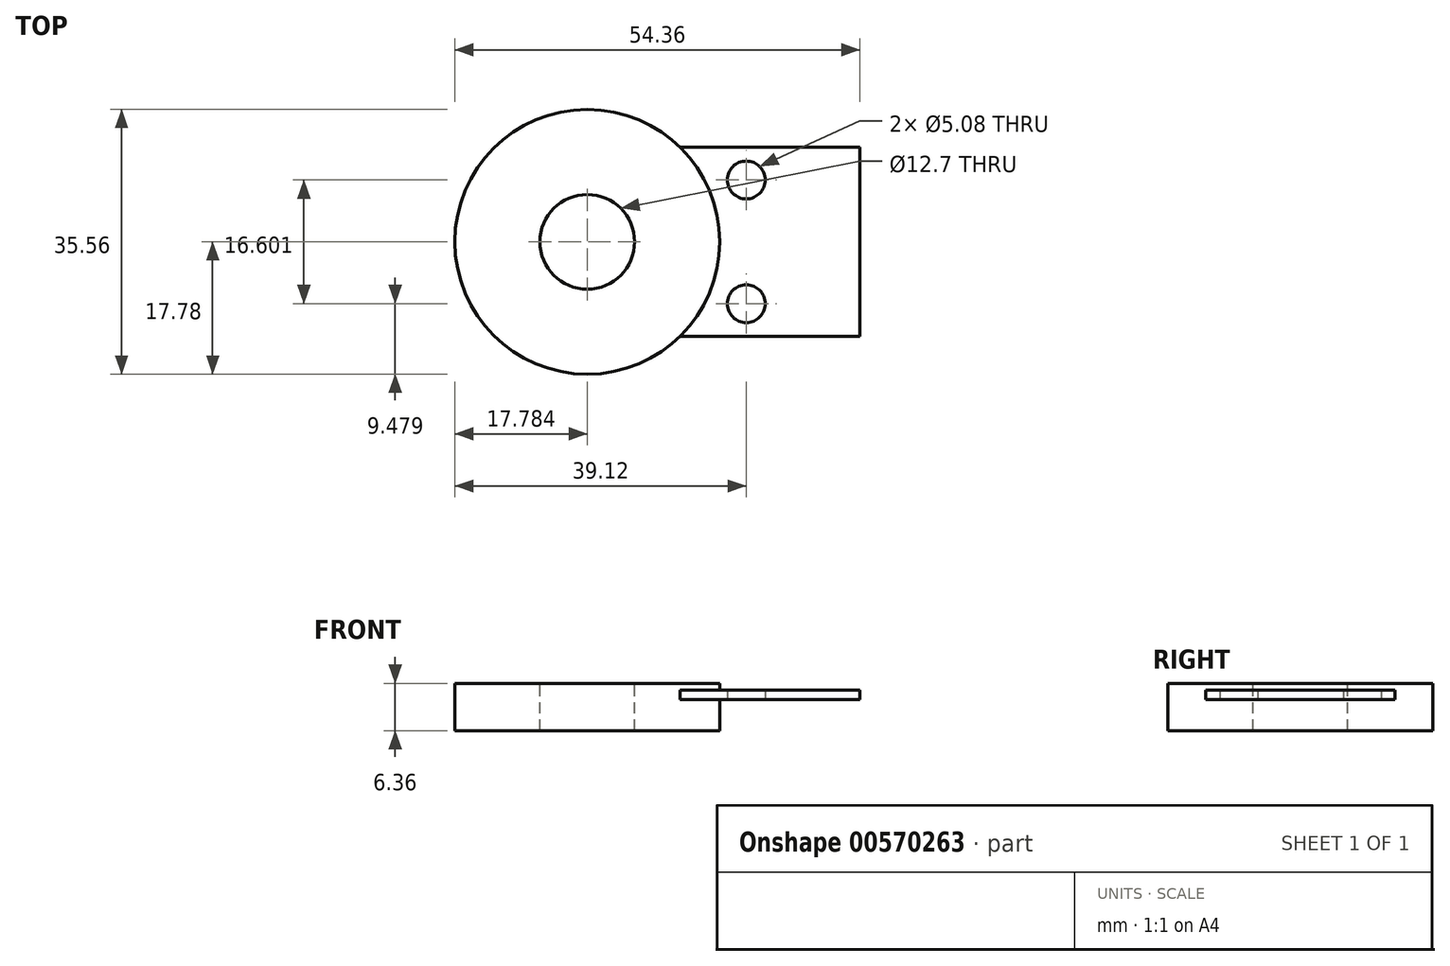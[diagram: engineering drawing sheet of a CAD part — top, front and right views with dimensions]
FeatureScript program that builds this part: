
annotation { "Feature Type Name" : "Feature", "Feature Type Description" : "" }
export const myFeature = defineFeature(function(context is Context, id is Id, definition is map)
    precondition{}
    {
        {
            var Q0;
            Q0=qCreatedBy(makeId("Front.planeOp"),FACE);
            var sketch = newSketch(context, id + "F0", { "sketchPlane" : qUnion([Q0])});
            skLineSegment(sketch, "E0.bottom", {"start": v(0, 2.29) * mm, "end": v(25.4, 2.29) * mm});
            skLineSegment(sketch, "E0.top", {"start": v(0, 1.02) * mm, "end": v(25.4, 1.02) * mm});
            skLineSegment(sketch, "E0.left", {"start": v(0, 2.29) * mm, "end": v(0, 1.02) * mm});
            skLineSegment(sketch, "E0.right", {"start": v(25.4, 2.29) * mm, "end": v(25.4, 1.02) * mm});
            skSolve(sketch);
        }
        {
            var Q0;
            Q0 = qSketchRegion(id + "F0", true);
            extrude(context, id + "F1", {"entities" : qUnion([Q0]), "endBound" : BoundingType.SYMMETRIC, "depth" : 25.4 * mm, "offsetDistance" : 25.4 * mm});
        }
        {
            var Q0;
            Q0=makeQuery(id+"F1.opExtrude","SWEPT_FACE",FACE,{"disambiguationData":[OSD([sQuery(id+"F0.wireOp",EDGE,"E0.top")])]});
            var sketch = newSketch(context, id + "F2", { "sketchPlane" : qUnion([Q0])});
            skCircle(sketch, "E1", {"center": v(10.16, 8.3) * mm, "radius": 2.54 * mm});
            skCircle(sketch, "E2", {"center": v(10.16, -8.3) * mm, "radius": 2.54 * mm});
            skSolve(sketch);
        }
        {
            var Q0;
            Q0 = qSketchRegion(id + "F2", true);
            extrude(context, id + "F3", {"entities" : qUnion([Q0]), "operationType" : NewBodyOperationType.REMOVE, "endBound" : BoundingType.THROUGH_ALL, "oppositeDirection" : true, "depth" : 25.4 * mm, "offsetDistance" : 25.4 * mm});
        }
        {
            var Q0;
            Q0=qCreatedBy(makeId("Top.planeOp"),FACE);
            var sketch = newSketch(context, id + "F4", { "sketchPlane" : qUnion([Q0])});
            skCircle(sketch, "E3", {"center": v(-11.18, 0) * mm, "radius": 17.78 * mm});
            skSolve(sketch);
        }
        {
            var Q0;
            Q0=makeQuery(id+"F4.imprint","IMPRINT",FACE,{"disambiguationData":[TD([[makeQuery(id+"F4.imprint","IMPRINT",EDGE,{"derivedFrom":sQuery(id+"F4.wireOp",EDGE,"E3")}),1.0]])]});
            extrude(context, id + "F5", {"entities" : qUnion([Q0]), "operationType" : NewBodyOperationType.ADD, "endBound" : BoundingType.SYMMETRIC, "depth" : 6.35 * mm, "offsetDistance" : 25.4 * mm});
        }
        {
            var Q0;
            Q0=makeQuery(id+"F5.opExtrude","CAP_FACE",FACE,{"disambiguationData":[OSD([sQuery(id+"F4.wireOp",EDGE,"E3")])],"isStart":false});
            var sketch = newSketch(context, id + "F6", { "sketchPlane" : qUnion([Q0])});
            skCircle(sketch, "E4", {"center": v(-11.18, 0) * mm, "radius": 6.35 * mm});
            skSolve(sketch);
        }
        {
            var Q0;
            Q0=makeQuery(id+"F6.imprint","IMPRINT",FACE,{"disambiguationData":[TD([[makeQuery(id+"F6.imprint","IMPRINT",EDGE,{"derivedFrom":sQuery(id+"F6.wireOp",EDGE,"E4")}),1.0]])]});
            extrude(context, id + "F7", {"entities" : qUnion([Q0]), "operationType" : NewBodyOperationType.REMOVE, "endBound" : BoundingType.THROUGH_ALL, "oppositeDirection" : true, "depth" : 25.4 * mm, "offsetDistance" : 25.4 * mm});
        }
    });
